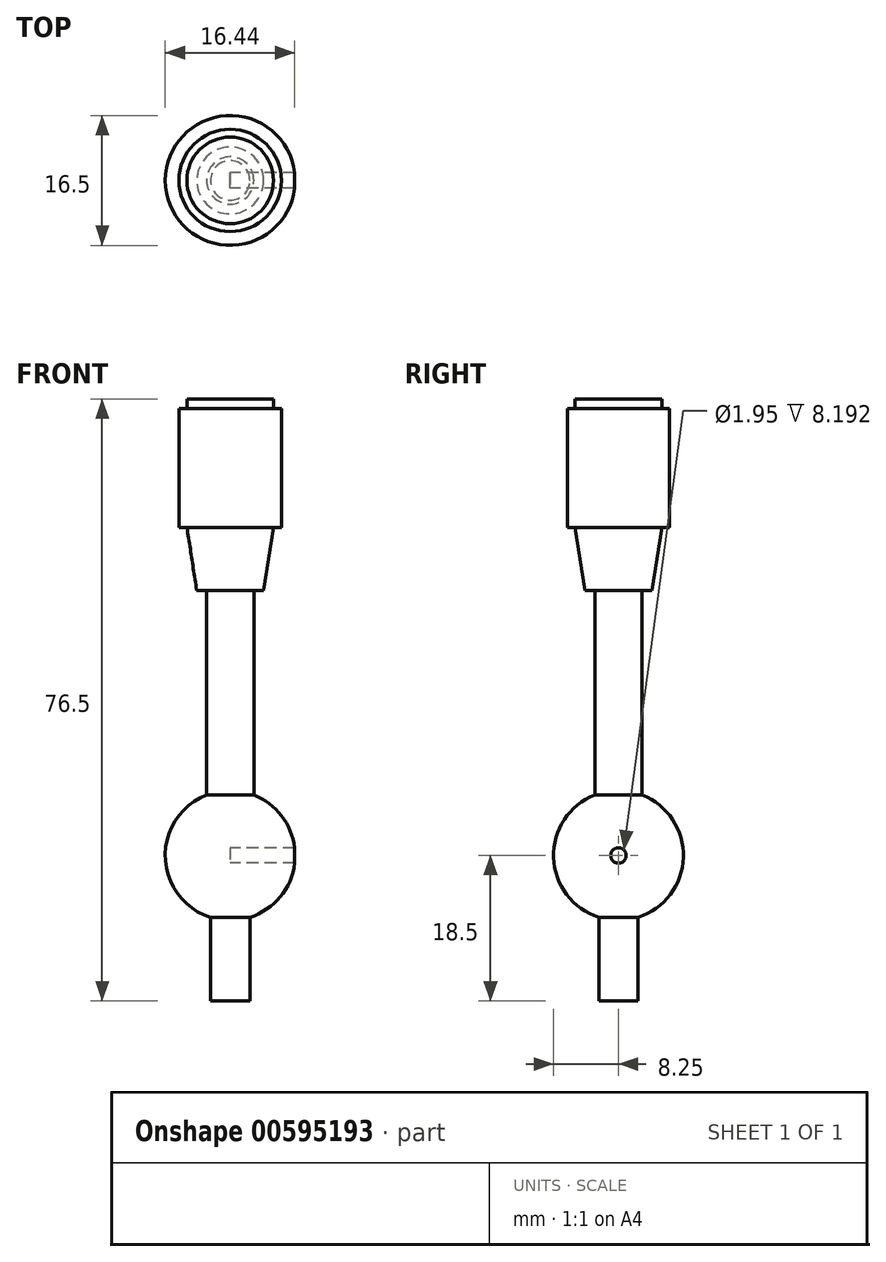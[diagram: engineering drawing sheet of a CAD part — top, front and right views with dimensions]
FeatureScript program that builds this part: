
annotation { "Feature Type Name" : "Feature", "Feature Type Description" : "" }
export const myFeature = defineFeature(function(context is Context, id is Id, definition is map)
    precondition{}
    {
        {
            var Q0;
            Q0=qCreatedBy(makeId("Front.planeOp"),FACE);
            var sketch = newSketch(context, id + "F0", { "sketchPlane" : qUnion([Q0])});
            skLineSegment(sketch, "E0", {"start": v(0, 0) * mm, "end": v(0, 58) * mm});
            skLineSegment(sketch, "E1", {"start": v(0, 0) * mm, "end": v(0, -18.5) * mm});
            skArc(sketch, "E2", {"start": v(-3, 7.69) * mm, "mid": v(-8.25, -0.27) * mm, "end": v(-2.5, -7.86) * mm});
            skPoint(sketch, "E3", {"position": v(0, 8.25) * mm});
            skPoint(sketch, "E4", {"position": v(0, -8.25) * mm});
            skPoint(sketch, "E5", {"position": v(-8.25, 0) * mm});
            skLineSegment(sketch, "E6", {"start": v(0, -18.5) * mm, "end": v(-2.5, -18.5) * mm});
            skLineSegment(sketch, "E7", {"start": v(-2.5, -18.5) * mm, "end": v(-2.5, -7.86) * mm});
            skLineSegment(sketch, "E8", {"start": v(-3, 7.69) * mm, "end": v(-3, 33.69) * mm});
            skLineSegment(sketch, "E9", {"start": v(-3, 33.69) * mm, "end": v(-4.25, 33.69) * mm});
            skLineSegment(sketch, "E10", {"start": v(-4.25, 33.69) * mm, "end": v(-5.5, 41.69) * mm});
            skPoint(sketch, "E11.end.orphan", {"position": v(0, 33.69) * mm});
            skLineSegment(sketch, "E12", {"start": v(0, 58) * mm, "end": v(-5.5, 58) * mm});
            skLineSegment(sketch, "E13", {"start": v(-5.5, 58) * mm, "end": v(-5.5, 56.75) * mm});
            skLineSegment(sketch, "E14", {"start": v(-5.5, 56.75) * mm, "end": v(-6.5, 56.75) * mm});
            skLineSegment(sketch, "E15", {"start": v(-6.5, 56.75) * mm, "end": v(-6.5, 41.69) * mm});
            skLineSegment(sketch, "E16", {"start": v(-6.5, 41.69) * mm, "end": v(-5.5, 41.69) * mm});
            skSolve(sketch);
        }
        {
            var Q0;
            Q0=makeQuery(id+"F0.imprint","IMPRINT",FACE,{"disambiguationData":[TD([[makeQuery(id+"F0.imprint","IMPRINT",EDGE,{"derivedFrom":sQuery(id+"F0.wireOp",EDGE,"E0")}),1.0]])]});
            var Q1;
            Q1=sQuery(id+"F0.wireOp",EDGE,"E0");
            revolve(context, id + "F1", {"entities" : qUnion([Q0]), "axis" : qUnion([Q1]), "revolveType" : RevolveType.ONE_DIRECTION, "angle" : 360 * degree});
        }
        {
            var Q0;
            Q0=qCreatedBy(makeId("Right.planeOp"),FACE);
            var sketch = newSketch(context, id + "F2", { "sketchPlane" : qUnion([Q0])});
            skCircle(sketch, "E17", {"center": v(0, 0) * mm, "radius": 1 * mm});
            skSolve(sketch);
        }
        {
            var Q0;
            Q0=sQuery(id+"F2.wireOp",VERTEX,"E17.center");
            var Q1;
            Q1=makeQuery(id+"F1.opRevolve","SWEPT_BODY",BODY,{"disambiguationData":[OSD([sQuery(id+"F0.wireOp",EDGE,"E0"),sQuery(id+"F0.wireOp",EDGE,"E1"),sQuery(id+"F0.wireOp",EDGE,"E2"),sQuery(id+"F0.wireOp",EDGE,"E6"),sQuery(id+"F0.wireOp",EDGE,"E7"),sQuery(id+"F0.wireOp",EDGE,"E8"),sQuery(id+"F0.wireOp",EDGE,"E9"),sQuery(id+"F0.wireOp",EDGE,"E10"),sQuery(id+"F0.wireOp",EDGE,"E12"),sQuery(id+"F0.wireOp",EDGE,"E13"),sQuery(id+"F0.wireOp",EDGE,"E14"),sQuery(id+"F0.wireOp",EDGE,"E15"),sQuery(id+"F0.wireOp",EDGE,"E16")])]});
            hole(context, id + "F3", {"style" : HoleStyle.SIMPLE, "endStyle" : HoleEndStyle.BLIND, "oppositeDirection" : true, "holeDiameter" : 1.95 * mm, "majorDiameter" : 5 * mm, "holeDepth" : 8.75 * mm, "isTappedThrough" : true, "tappedDepth" : 12 * mm, "tapClearance" : 3, "startFromSketch" : true, "locations" : qUnion([Q0]), "scope" : qUnion([Q1])});
        }
    });
